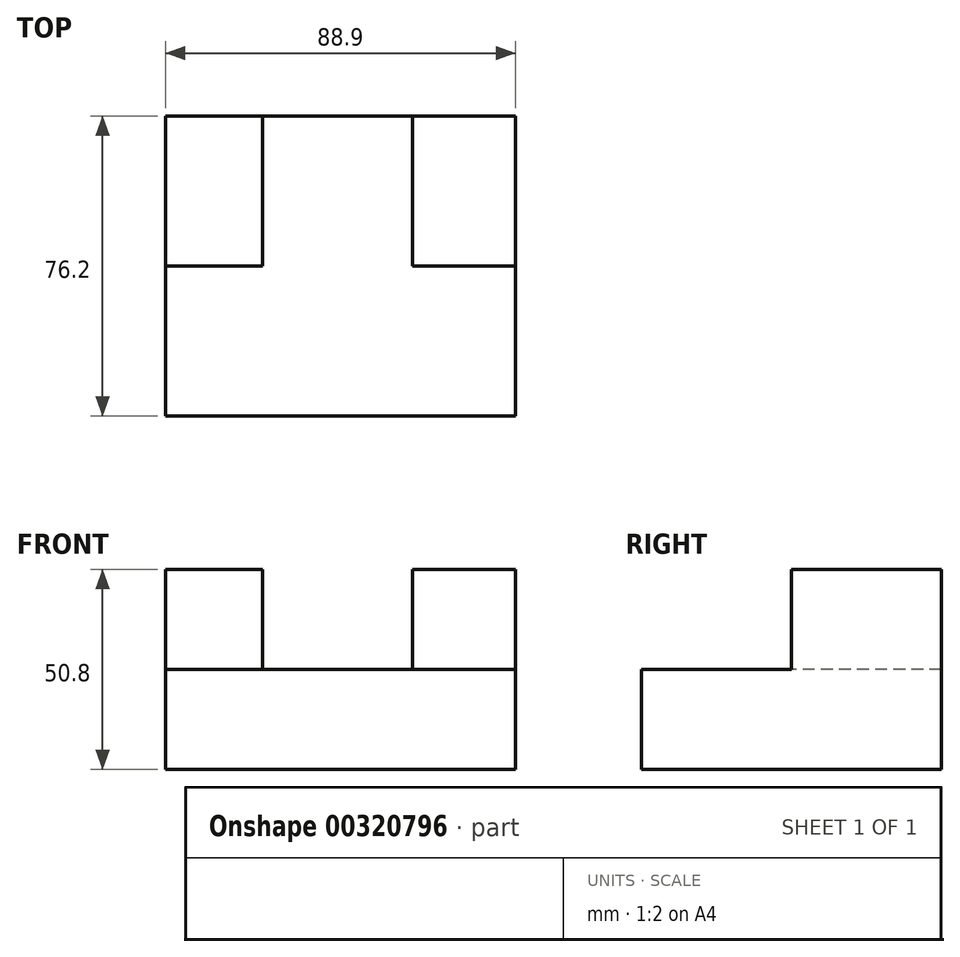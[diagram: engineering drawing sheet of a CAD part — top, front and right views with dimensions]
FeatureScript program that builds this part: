
annotation { "Feature Type Name" : "Feature", "Feature Type Description" : "" }
export const myFeature = defineFeature(function(context is Context, id is Id, definition is map)
    precondition{}
    {
        {
            var Q0;
            Q0=qCreatedBy(makeId("Right.planeOp"),FACE);
            var sketch = newSketch(context, id + "F0", { "sketchPlane" : qUnion([Q0])});
            skLineSegment(sketch, "E0", {"start": v(-40.1, -10.72) * mm, "end": v(-40.1, -36.12) * mm});
            skLineSegment(sketch, "E1", {"start": v(-40.1, -36.12) * mm, "end": v(36.1, -36.12) * mm});
            skLineSegment(sketch, "E2", {"start": v(36.1, -36.12) * mm, "end": v(36.1, 14.68) * mm});
            skLineSegment(sketch, "E3", {"start": v(36.1, 14.68) * mm, "end": v(-2, 14.68) * mm});
            skLineSegment(sketch, "E4", {"start": v(-2, 14.68) * mm, "end": v(-2, -10.72) * mm});
            skLineSegment(sketch, "E5", {"start": v(-2, -10.72) * mm, "end": v(-40.1, -10.72) * mm});
            skSolve(sketch);
        }
        {
            var Q0;
            Q0=makeQuery(id+"F0.imprint","IMPRINT",FACE,{"disambiguationData":[TD([[makeQuery(id+"F0.imprint","IMPRINT",EDGE,{"derivedFrom":sQuery(id+"F0.wireOp",EDGE,"E0")}),1.0]])]});
            extrude(context, id + "F1", {"entities" : qUnion([Q0]), "depth" : 88.9 * mm});
        }
        {
            var Q0;
            Q0=makeQuery(id+"F1.opExtrude","SWEPT_FACE",FACE,{"disambiguationData":[OSD([sQuery(id+"F0.wireOp",EDGE,"E4")])]});
            var sketch = newSketch(context, id + "F2", { "sketchPlane" : qUnion([Q0])});
            skLineSegment(sketch, "E6", {"start": v(24.6, 14.68) * mm, "end": v(24.6, -10.72) * mm});
            skLineSegment(sketch, "E7", {"start": v(24.6, -10.72) * mm, "end": v(62.7, -10.72) * mm});
            skLineSegment(sketch, "E8", {"start": v(62.7, -10.72) * mm, "end": v(62.7, 14.68) * mm});
            skLineSegment(sketch, "E9", {"start": v(62.7, 14.68) * mm, "end": v(24.6, 14.68) * mm});
            skSolve(sketch);
        }
        {
            var Q0;
            Q0=makeQuery(id+"F2.imprint","IMPRINT",FACE,{"disambiguationData":[TD([[makeQuery(id+"F2.imprint","IMPRINT",EDGE,{"derivedFrom":sQuery(id+"F2.wireOp",EDGE,"E6")}),1.0]])]});
            extrude(context, id + "F3", {"entities" : qUnion([Q0]), "operationType" : NewBodyOperationType.REMOVE, "endBound" : BoundingType.THROUGH_ALL, "oppositeDirection" : true, "depth" : 25.4 * mm});
        }
    });
